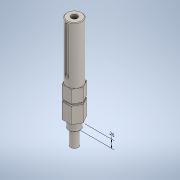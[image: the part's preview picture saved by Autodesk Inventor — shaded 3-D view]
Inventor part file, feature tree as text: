
AUTODESK INVENTOR PART (.ipt)
format: ipt  version: 2020.2 (Build 242310000, 310)  size: 144,384 bytes
history: native  units: in
note: dims shown in document units (in); Inventor stores cm internally (conversion verified against a paired STEP export)
features: other x3, extrude x1, sketch x1
ambient origin geometry x8: Origin, YZ Plane, XZ Plane, XY Plane, X Axis, Y Axis, Z Axis, Center Point
bodies: Solid1 (feature_tree)
feature tree (5):
  other  "Annotations"
  extrude  "Extrusion1"  Depth=0.5in TaperAngle=0.0deg
  sketch  "Sketch1"  dims[d1=0.25in d2=0.5in d3=0.0in d0=0.26in]
  other  "1_4-20 Tapped Hole1"
  other  "Linear Dimension 1"
